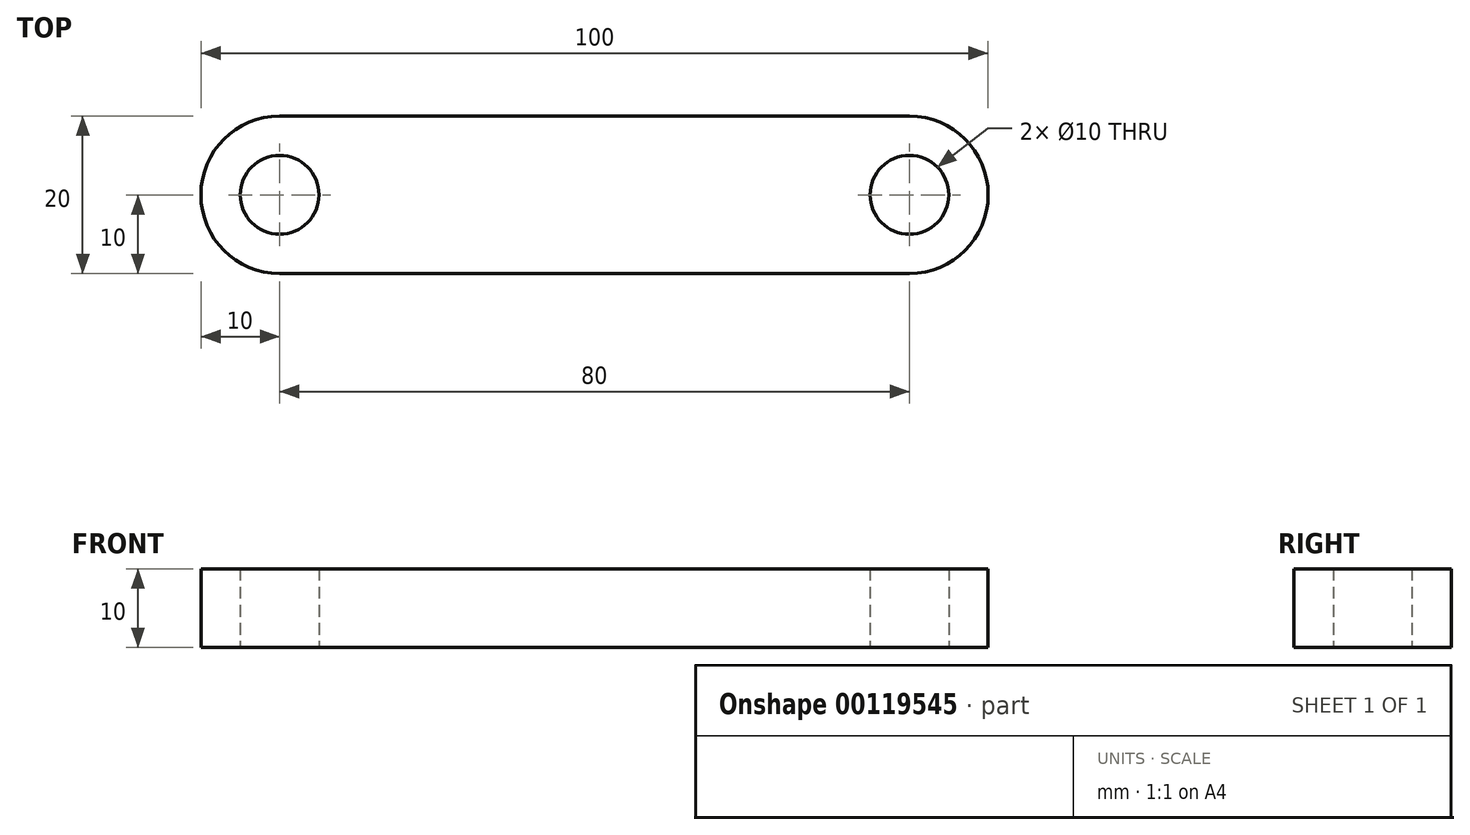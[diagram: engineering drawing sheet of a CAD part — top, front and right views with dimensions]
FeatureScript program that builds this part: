
annotation { "Feature Type Name" : "Feature", "Feature Type Description" : "" }
export const myFeature = defineFeature(function(context is Context, id is Id, definition is map)
    precondition{}
    {
        {
            var Q0;
            Q0=qCreatedBy(makeId("Top.planeOp"),FACE);
            var sketch = newSketch(context, id + "F0", { "sketchPlane" : qUnion([Q0])});
            skLineSegment(sketch, "E0.bottom", {"start": v(-40, -10) * mm, "end": v(40, -10) * mm});
            skLineSegment(sketch, "E0.top", {"start": v(-40, 10) * mm, "end": v(40, 10) * mm});
            skPoint(sketch, "E0.middle", {"position": v(0, 0) * mm});
            skArc(sketch, "E1", {"start": v(-40, 10) * mm, "mid": v(-50, 0) * mm, "end": v(-40, -10) * mm});
            skArc(sketch, "E2", {"start": v(40, -10) * mm, "mid": v(50, 0) * mm, "end": v(40, 10) * mm});
            skCircle(sketch, "E3", {"center": v(-40, 0) * mm, "radius": 5 * mm});
            skCircle(sketch, "E4", {"center": v(40, 0) * mm, "radius": 5 * mm});
            skSolve(sketch);
        }
        {
            var Q0;
            Q0=makeQuery(id+"F0.imprint","IMPRINT",FACE,{"disambiguationData":[TD([[makeQuery(id+"F0.imprint","IMPRINT",EDGE,{"derivedFrom":sQuery(id+"F0.wireOp",EDGE,"E0.bottom")}),1.0]])]});
            extrude(context, id + "F1", {"entities" : qUnion([Q0]), "endBound" : BoundingType.SYMMETRIC, "depth" : 10 * mm});
        }
    });
